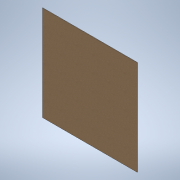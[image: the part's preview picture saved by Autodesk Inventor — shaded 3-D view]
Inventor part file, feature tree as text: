
AUTODESK INVENTOR PART (.ipt)
format: ipt  version: 2022 (Build 260153000, 153)  size: 112,128 bytes
history: native  units: mm
features: other x1, extrude x1, sketch x1
ambient origin geometry x8: Origin, YZ Plane, XZ Plane, XY Plane, X Axis, Y Axis, Z Axis, Center Point
bodies: Body1 (feature_tree)
feature tree (3):
  other  "Sólido1"
  extrude  "Extrusão1"  Depth=600.0mm
  sketch  "Esboço1"  dims[d0=600.0mm d1=600.0mm d2=3.0mm d3=0.0mm]
